# Revit family: M_Ceiling Valve_Ceiling Based
name_source: partatom
category: Specialty Equipment
revit_build: Autodesk Revit 2015 (Build: 20160512_0715(x64)
units: mm (PartAtom-declared; Revit-internal decimal feet)

## types (10) — shared parameters
Description = Firefly 102 - 80mm Fire Rated Ceiling Valve Supply
IFC Classification = Building Element Proxy
InsideRadius = 60 mm  [stored 0.19685 ft]
Manufacturer = Tenmat ltd
Material = Intumescent Sealant
OutsideRadius = 62 mm  [stored 0.203412 ft]
Performance = BS EN 1366-3:2009 & BS 476, ETA-12/0332, 1224-CPR-0341, CE Marked
URL = https://www.tenmat.com
Youtube clip = https://www.youtube.com

## per-type parameters (varying)
| type | Cut_Out_Rad | Disc_Rad | Extract_Valve | Holder_Depth | Overall_Rad | Supply_Valve | Valve_Rad |
| Supply - 80mm | 47 mm | 41 mm | Yes | 30 mm  [stored 0.0984252 ft] | 58 mm  [stored 0.190289 ft] | Yes | 40 mm  [stored 0.131234 ft] |
| Supply - 100mm | 59 mm | 48 mm  [stored 0.15748 ft] | No | 30 mm  [stored 0.0984252 ft] | 70 mm  [stored 0.229659 ft] | Yes | 52 mm  [stored 0.170604 ft] |
| Supply - 125mm | 74 mm | 57 mm  [stored 0.187008 ft] | No | 36 mm  [stored 0.11811 ft] | 85 mm  [stored 0.278871 ft] | Yes | 67 mm  [stored 0.219816 ft] |
| Supply - 150mm | 90 mm | 69 mm | No | 44 mm  [stored 0.144357 ft] | 101 mm  [stored 0.331365 ft] | Yes | 83 mm  [stored 0.27231 ft] |
| Supply - 200mm | 116 mm | 100 mm  [stored 0.328084 ft] | No | 54 mm  [stored 0.177165 ft] | 127 mm | Yes | 109 mm  [stored 0.357612 ft] |
| Extract - 80mm | 47 mm | 41 mm | Yes | 30 mm  [stored 0.0984252 ft] | 58 mm  [stored 0.190289 ft] | No | 40 mm  [stored 0.131234 ft] |
| Extract - 100mm | 59 mm | 48 mm  [stored 0.15748 ft] | Yes | 30 mm  [stored 0.0984252 ft] | 70 mm  [stored 0.229659 ft] | No | 52 mm  [stored 0.170604 ft] |
| Extract - 125mm | 74 mm | 57 mm  [stored 0.187008 ft] | Yes | 36 mm  [stored 0.11811 ft] | 85 mm  [stored 0.278871 ft] | No | 67 mm  [stored 0.219816 ft] |
| Extract - 150mm | 90 mm | 69 mm | Yes | 44 mm  [stored 0.144357 ft] | 101 mm  [stored 0.331365 ft] | No | 83 mm  [stored 0.27231 ft] |
| Extract - 200mm | 116 mm | 100 mm  [stored 0.328084 ft] | Yes | 54 mm  [stored 0.177165 ft] | 127 mm | No | 109 mm  [stored 0.357612 ft] |

note: [stored X ft] marks values corroborated as IEEE doubles in the binary element streams (Revit-internal decimal feet)

## geometry (parser evidence)
native form markers: Blend x2, Sweep x3
no freeform markers — native parametric forms only
